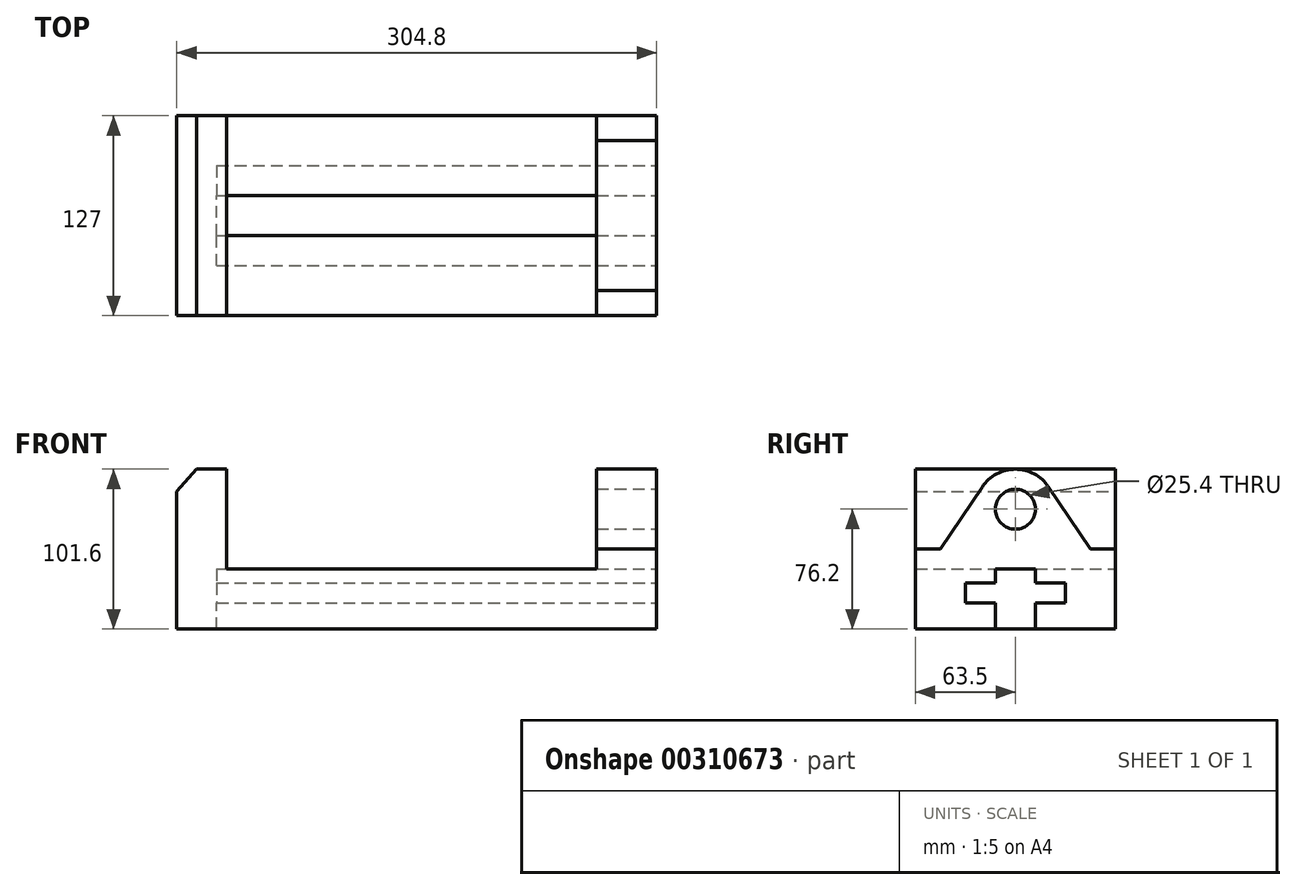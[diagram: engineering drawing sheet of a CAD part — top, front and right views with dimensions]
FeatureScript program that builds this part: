
annotation { "Feature Type Name" : "Feature", "Feature Type Description" : "" }
export const myFeature = defineFeature(function(context is Context, id is Id, definition is map)
    precondition{}
    {
        {
            var Q0;
            Q0=qCreatedBy(makeId("Front.planeOp"),FACE);
            var sketch = newSketch(context, id + "F0", { "sketchPlane" : qUnion([Q0])});
            skLineSegment(sketch, "E0", {"start": v(31.75, 38.1) * mm, "end": v(266.7, 38.1) * mm});
            skLineSegment(sketch, "E1", {"start": v(266.7, 38.1) * mm, "end": v(266.7, 101.6) * mm});
            skLineSegment(sketch, "E2", {"start": v(266.7, 101.6) * mm, "end": v(304.8, 101.6) * mm});
            skLineSegment(sketch, "E3", {"start": v(304.8, 101.6) * mm, "end": v(304.8, 0) * mm});
            skLineSegment(sketch, "E4", {"start": v(304.8, 0) * mm, "end": v(0, 0) * mm});
            skLineSegment(sketch, "E5", {"start": v(0, 0) * mm, "end": v(0, 87.4) * mm});
            skLineSegment(sketch, "E6", {"start": v(0, 87.4) * mm, "end": v(12.7, 101.6) * mm});
            skLineSegment(sketch, "E7", {"start": v(12.7, 101.6) * mm, "end": v(31.75, 101.6) * mm});
            skLineSegment(sketch, "E8", {"start": v(31.75, 101.6) * mm, "end": v(31.75, 38.1) * mm});
            skSolve(sketch);
        }
        {
            var Q0;
            Q0 = qSketchRegion(id + "F0", true);
            extrude(context, id + "F1", {"entities" : qUnion([Q0]), "depth" : 127 * mm});
        }
        {
            var Q0;
            Q0=makeQuery(id+"F1.opExtrude","SWEPT_FACE",FACE,{"disambiguationData":[OSD([sQuery(id+"F0.wireOp",EDGE,"E3")])]});
            var sketch = newSketch(context, id + "F2", { "sketchPlane" : qUnion([Q0])});
            skLineSegment(sketch, "E9", {"start": v(-76.2, 0) * mm, "end": v(-76.2, 16.5) * mm});
            skLineSegment(sketch, "E10", {"start": v(-76.2, 16.5) * mm, "end": v(-95.25, 16.5) * mm});
            skLineSegment(sketch, "E11", {"start": v(-95.25, 16.5) * mm, "end": v(-95.25, 29.2) * mm});
            skLineSegment(sketch, "E12", {"start": v(-95.25, 29.2) * mm, "end": v(-76.2, 29.2) * mm});
            skLineSegment(sketch, "E13", {"start": v(-76.2, 29.2) * mm, "end": v(-76.2, 38.1) * mm});
            skLineSegment(sketch, "E14", {"start": v(-76.2, 38.1) * mm, "end": v(-50.8, 38.1) * mm});
            skLineSegment(sketch, "E15", {"start": v(-50.8, 38.1) * mm, "end": v(-50.8, 29.2) * mm});
            skLineSegment(sketch, "E16", {"start": v(-50.8, 29.2) * mm, "end": v(-31.75, 29.2) * mm});
            skLineSegment(sketch, "E17", {"start": v(-31.75, 29.2) * mm, "end": v(-31.75, 16.5) * mm});
            skLineSegment(sketch, "E18", {"start": v(-31.75, 16.5) * mm, "end": v(-50.8, 16.5) * mm});
            skLineSegment(sketch, "E19", {"start": v(-50.8, 16.5) * mm, "end": v(-50.8, 0) * mm});
            skLineSegment(sketch, "E20", {"start": v(-127, 50.8) * mm, "end": v(-111.12, 50.8) * mm});
            skLineSegment(sketch, "E21", {"start": v(-111.12, 50.8) * mm, "end": v(-84.6, 90.35) * mm});
            skLineSegment(sketch, "E22", {"start": v(-42.4, 90.35) * mm, "end": v(-15.87, 50.8) * mm});
            skLineSegment(sketch, "E23", {"start": v(-15.88, 50.8) * mm, "end": v(0, 50.8) * mm});
            skArc(sketch, "E24", {"start": v(-42.4, 90.35) * mm, "mid": v(-63.5, 101.6) * mm, "end": v(-84.6, 90.35) * mm});
            skLineSegment(sketch, "E25", {"start": v(-63.5, 101.6) * mm, "end": v(-63.5, 0) * mm, "construction": true});
            skCircle(sketch, "E26", {"center": v(-63.5, 76.2) * mm, "radius": 12.7 * mm});
            skSolve(sketch);
        }
        {
            var Q0;
            {var subQ7=sQuery(id+"F2.wireOp",EDGE,"E20");Q0=makeQuery(id+"F2.imprint","IMPRINT",FACE,{"disambiguationData":[TD([[makeQuery(id+"F2.imprint","IMPRINT",EDGE,{"derivedFrom":subQ7}),1.0]])]});}
            var Q1;
            {var subQ1=sQuery(id+"F2.wireOp",EDGE,"E22");Q1=makeQuery(id+"F2.imprint","IMPRINT",FACE,{"disambiguationData":[TD([[makeQuery(id+"F2.imprint","IMPRINT",EDGE,{"derivedFrom":subQ1}),1.0]])]});}
            extrude(context, id + "F3", {"entities" : qUnion([Q0, Q1]), "operationType" : NewBodyOperationType.REMOVE, "oppositeDirection" : true, "depth" : 76.2 * mm});
        }
        {
            var Q0;
            Q0=makeQuery(id+"F2.imprint","IMPRINT",FACE,{"disambiguationData":[TD([[makeQuery(id+"F2.imprint","IMPRINT",EDGE,{"derivedFrom":sQuery(id+"F2.wireOp",EDGE,"E26")}),1.0]])]});
            extrude(context, id + "F4", {"entities" : qUnion([Q0]), "operationType" : NewBodyOperationType.REMOVE, "oppositeDirection" : true, "depth" : 76.2 * mm});
        }
        {
            var Q0;
            {var subQ0=sQuery(id+"F2.wireOp",EDGE,"E9");Q0=makeQuery(id+"F2.imprint","IMPRINT",FACE,{"disambiguationData":[TD([[makeQuery(id+"F2.imprint","IMPRINT",EDGE,{"derivedFrom":subQ0}),-1.0]])]});}
            extrude(context, id + "F5", {"entities" : qUnion([Q0]), "operationType" : NewBodyOperationType.REMOVE, "oppositeDirection" : true, "depth" : 279.4 * mm});
        }
    });
